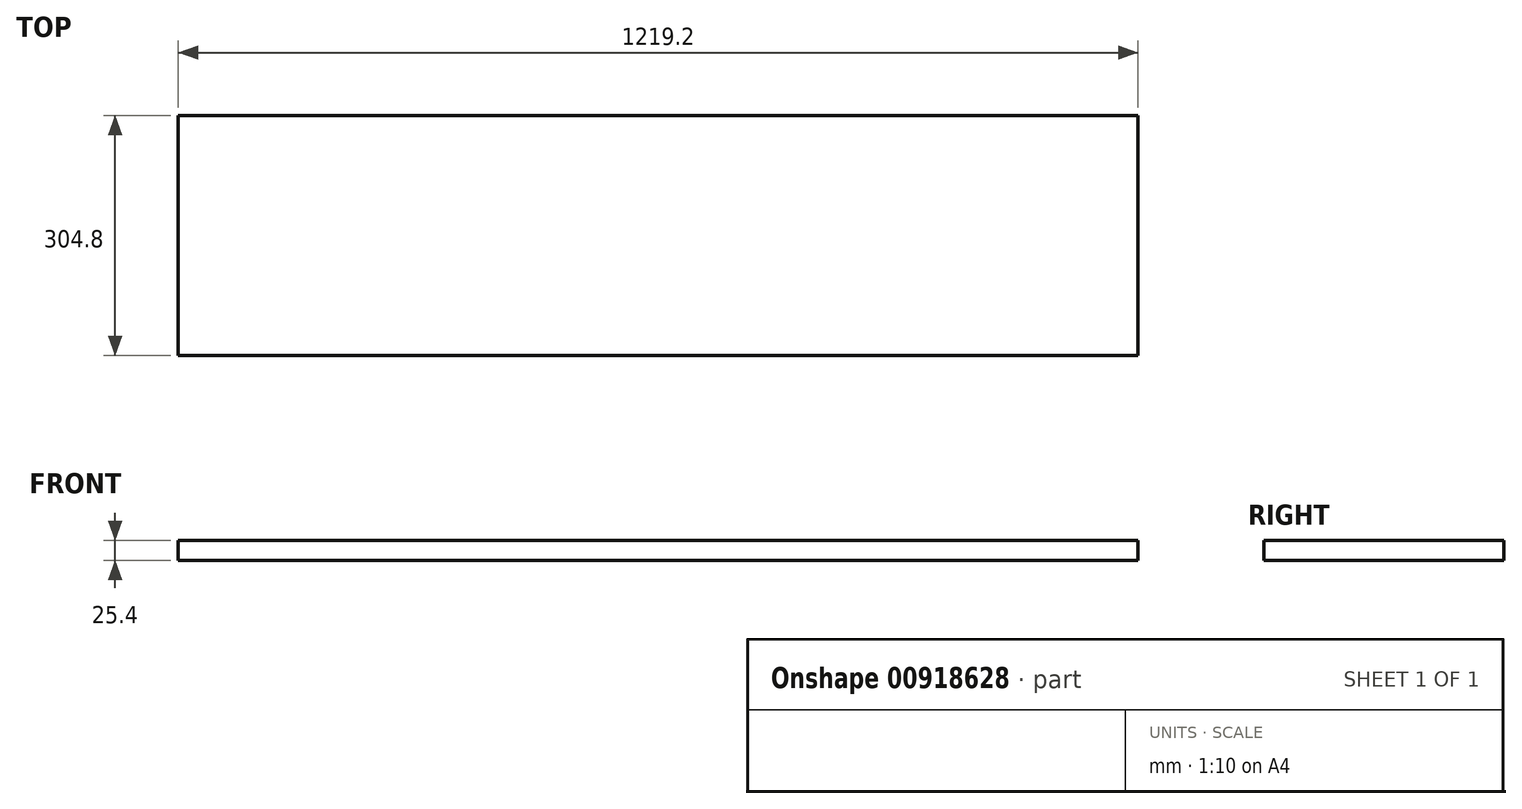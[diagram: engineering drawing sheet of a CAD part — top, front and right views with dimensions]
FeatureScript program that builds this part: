
annotation { "Feature Type Name" : "Feature", "Feature Type Description" : "" }
export const myFeature = defineFeature(function(context is Context, id is Id, definition is map)
    precondition{}
    {
        {
            var Q0;
            Q0=qCreatedBy(makeId("Front.planeOp"),FACE);
            var sketch = newSketch(context, id + "F0", { "sketchPlane" : qUnion([Q0])});
            skLineSegment(sketch, "E0.bottom", {"start": v(-609.6, 12.7) * mm, "end": v(609.6, 12.7) * mm});
            skLineSegment(sketch, "E0.top", {"start": v(-609.6, -12.7) * mm, "end": v(609.6, -12.7) * mm});
            skLineSegment(sketch, "E0.left", {"start": v(-609.6, 12.7) * mm, "end": v(-609.6, -12.7) * mm});
            skLineSegment(sketch, "E0.right", {"start": v(609.6, 12.7) * mm, "end": v(609.6, -12.7) * mm});
            skLineSegment(sketch, "E1", {"start": v(-609.6, -12.7) * mm, "end": v(609.6, 12.7) * mm, "construction": true});
            skSolve(sketch);
        }
        {
            var Q0;
            Q0=makeQuery(id+"F0.imprint","IMPRINT",FACE,{"disambiguationData":[TD([[makeQuery(id+"F0.imprint","IMPRINT",EDGE,{"derivedFrom":sQuery(id+"F0.wireOp",EDGE,"E0.bottom")}),-1.0]])]});
            extrude(context, id + "F1", {"entities" : qUnion([Q0]), "depth" : 304.8 * mm, "offsetDistance" : 25.4 * mm});
        }
    });
